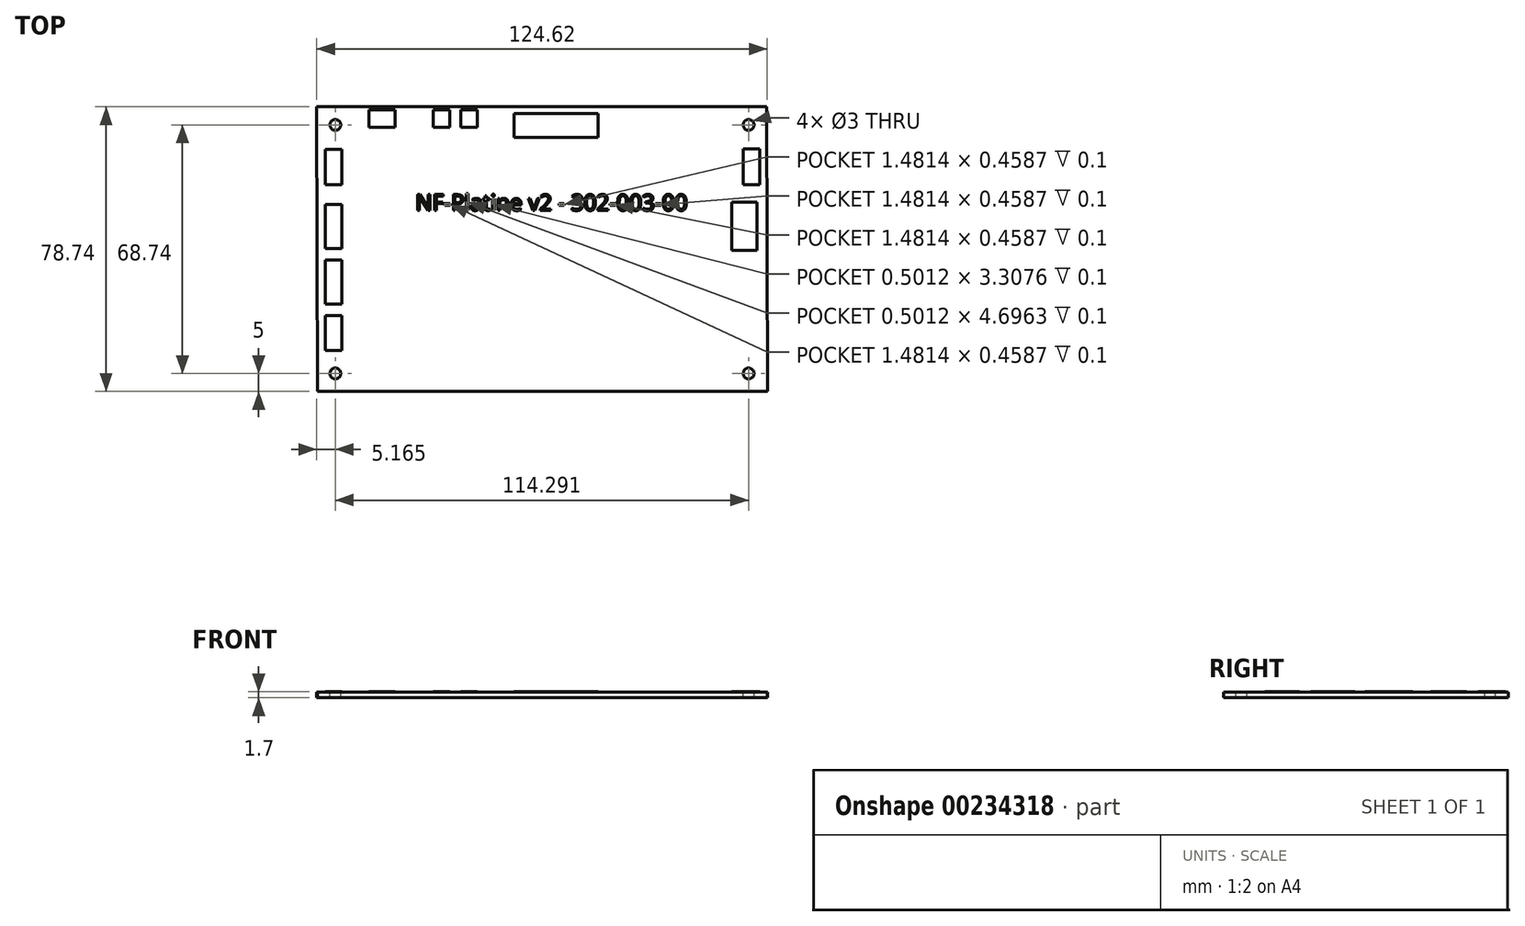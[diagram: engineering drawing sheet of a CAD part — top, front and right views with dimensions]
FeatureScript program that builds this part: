
annotation { "Feature Type Name" : "Feature", "Feature Type Description" : "" }
export const myFeature = defineFeature(function(context is Context, id is Id, definition is map)
    precondition{}
    {
        {
            var Q0;
            Q0=qCreatedBy(makeId("Top.planeOp"),FACE);
            var sketch = newSketch(context, id + "F0", { "sketchPlane" : qUnion([Q0])});
            skLineSegment(sketch, "E0.bottom", {"start": v(62.31, -39.37) * mm, "end": v(-62.15, -39.37) * mm});
            skLineSegment(sketch, "E0.top", {"start": v(62.15, 39.37) * mm, "end": v(-62.31, 39.37) * mm});
            skLineSegment(sketch, "E0.left", {"start": v(62.31, -39.37) * mm, "end": v(62.15, 39.37) * mm});
            skLineSegment(sketch, "E0.right", {"start": v(-62.15, -39.37) * mm, "end": v(-62.31, 39.37) * mm});
            skPoint(sketch, "E0.middle", {"position": v(0, 0) * mm});
            skCircle(sketch, "E1", {"center": v(-57.15, -34.37) * mm, "radius": 1.5 * mm});
            skCircle(sketch, "E2.MirrorC", {"center": v(57.15, -34.37) * mm, "radius": 1.5 * mm});
            skCircle(sketch, "E3.MirrorC", {"center": v(-57.15, 34.37) * mm, "radius": 1.5 * mm});
            skCircle(sketch, "E4.MirrorC", {"center": v(57.15, 34.37) * mm, "radius": 1.5 * mm});
            skLineSegment(sketch, "E5.bottom", {"start": v(-59.91, 27.62) * mm, "end": v(-55.3, 27.62) * mm});
            skLineSegment(sketch, "E5.top", {"start": v(-59.91, 17.86) * mm, "end": v(-55.3, 17.86) * mm});
            skLineSegment(sketch, "E5.left", {"start": v(-59.91, 27.62) * mm, "end": v(-59.91, 17.86) * mm});
            skLineSegment(sketch, "E5.right", {"start": v(-55.3, 27.62) * mm, "end": v(-55.3, 17.86) * mm});
            skLineSegment(sketch, "E6.bottom", {"start": v(-59.91, 12.38) * mm, "end": v(-55.3, 12.38) * mm});
            skLineSegment(sketch, "E6.top", {"start": v(-59.91, 0.12) * mm, "end": v(-55.3, 0.12) * mm});
            skLineSegment(sketch, "E6.left", {"start": v(-59.91, 12.38) * mm, "end": v(-59.91, 0.12) * mm});
            skLineSegment(sketch, "E6.right", {"start": v(-55.3, 12.38) * mm, "end": v(-55.3, 0.12) * mm});
            skLineSegment(sketch, "E7.bottom", {"start": v(-59.91, -3) * mm, "end": v(-55.3, -3) * mm});
            skLineSegment(sketch, "E7.top", {"start": v(-59.91, -15.22) * mm, "end": v(-55.3, -15.22) * mm});
            skLineSegment(sketch, "E7.left", {"start": v(-59.91, -3) * mm, "end": v(-59.91, -15.22) * mm});
            skLineSegment(sketch, "E7.right", {"start": v(-55.3, -3) * mm, "end": v(-55.3, -15.22) * mm});
            skLineSegment(sketch, "E8.bottom", {"start": v(-59.91, -18.36) * mm, "end": v(-55.3, -18.36) * mm});
            skLineSegment(sketch, "E8.top", {"start": v(-59.91, -27.98) * mm, "end": v(-55.3, -27.98) * mm});
            skLineSegment(sketch, "E8.left", {"start": v(-59.91, -18.36) * mm, "end": v(-59.91, -27.98) * mm});
            skLineSegment(sketch, "E8.right", {"start": v(-55.3, -18.36) * mm, "end": v(-55.3, -27.98) * mm});
            skLineSegment(sketch, "E9.bottom", {"start": v(-47.83, 38.6) * mm, "end": v(-40.65, 38.6) * mm});
            skLineSegment(sketch, "E9.top", {"start": v(-47.83, 33.77) * mm, "end": v(-40.65, 33.77) * mm});
            skLineSegment(sketch, "E9.left", {"start": v(-47.83, 38.6) * mm, "end": v(-47.83, 33.77) * mm});
            skLineSegment(sketch, "E9.right", {"start": v(-40.65, 38.6) * mm, "end": v(-40.65, 33.77) * mm});
            skLineSegment(sketch, "E10.bottom", {"start": v(-30.04, 38.6) * mm, "end": v(-25.46, 38.6) * mm});
            skLineSegment(sketch, "E10.top", {"start": v(-30.04, 33.77) * mm, "end": v(-25.46, 33.77) * mm});
            skLineSegment(sketch, "E10.left", {"start": v(-30.04, 38.6) * mm, "end": v(-30.04, 33.77) * mm});
            skLineSegment(sketch, "E10.right", {"start": v(-25.46, 38.6) * mm, "end": v(-25.46, 33.77) * mm});
            skLineSegment(sketch, "E11.bottom", {"start": v(-22.44, 38.6) * mm, "end": v(-17.86, 38.6) * mm});
            skLineSegment(sketch, "E11.top", {"start": v(-22.44, 33.77) * mm, "end": v(-17.86, 33.77) * mm});
            skLineSegment(sketch, "E11.left", {"start": v(-22.44, 38.6) * mm, "end": v(-22.44, 33.77) * mm});
            skLineSegment(sketch, "E11.right", {"start": v(-17.86, 38.6) * mm, "end": v(-17.86, 33.77) * mm});
            skLineSegment(sketch, "E12.bottom", {"start": v(15.53, 30.95) * mm, "end": v(-7.67, 30.95) * mm});
            skLineSegment(sketch, "E12.top", {"start": v(15.53, 37.47) * mm, "end": v(-7.67, 37.47) * mm});
            skLineSegment(sketch, "E12.left", {"start": v(15.53, 30.95) * mm, "end": v(15.53, 37.47) * mm});
            skLineSegment(sketch, "E12.right", {"start": v(-7.67, 30.95) * mm, "end": v(-7.67, 37.47) * mm});
            skLineSegment(sketch, "E13.bottom", {"start": v(55.65, 27.78) * mm, "end": v(60.23, 27.78) * mm});
            skLineSegment(sketch, "E13.top", {"start": v(55.65, 17.86) * mm, "end": v(60.23, 17.86) * mm});
            skLineSegment(sketch, "E13.left", {"start": v(55.65, 27.78) * mm, "end": v(55.65, 17.86) * mm});
            skLineSegment(sketch, "E13.right", {"start": v(60.23, 27.78) * mm, "end": v(60.23, 17.86) * mm});
            skLineSegment(sketch, "E14.bottom", {"start": v(52.5, 13.03) * mm, "end": v(59.41, 13.03) * mm});
            skLineSegment(sketch, "E14.top", {"start": v(52.5, -0.3) * mm, "end": v(59.41, -0.3) * mm});
            skLineSegment(sketch, "E14.left", {"start": v(52.5, 13.03) * mm, "end": v(52.5, -0.3) * mm});
            skLineSegment(sketch, "E14.right", {"start": v(59.41, 13.03) * mm, "end": v(59.41, -0.3) * mm});
            skSolve(sketch);
        }
        {
            var Q0;
            Q0=makeQuery(id+"F0.imprint","IMPRINT",FACE,{"disambiguationData":[TD([[makeQuery(id+"F0.imprint","IMPRINT",EDGE,{"derivedFrom":sQuery(id+"F0.wireOp",EDGE,"E0.bottom")}),-1.0]])]});
            var Q1;
            Q1=makeQuery(id+"F0.imprint","IMPRINT",FACE,{"disambiguationData":[TD([[makeQuery(id+"F0.imprint","IMPRINT",EDGE,{"derivedFrom":sQuery(id+"F0.wireOp",EDGE,"E5.bottom")}),-1.0]])]});
            var Q2;
            Q2=makeQuery(id+"F0.imprint","IMPRINT",FACE,{"disambiguationData":[TD([[makeQuery(id+"F0.imprint","IMPRINT",EDGE,{"derivedFrom":sQuery(id+"F0.wireOp",EDGE,"E6.bottom")}),-1.0]])]});
            var Q3;
            Q3=makeQuery(id+"F0.imprint","IMPRINT",FACE,{"disambiguationData":[TD([[makeQuery(id+"F0.imprint","IMPRINT",EDGE,{"derivedFrom":sQuery(id+"F0.wireOp",EDGE,"E7.bottom")}),-1.0]])]});
            var Q4;
            Q4=makeQuery(id+"F0.imprint","IMPRINT",FACE,{"disambiguationData":[TD([[makeQuery(id+"F0.imprint","IMPRINT",EDGE,{"derivedFrom":sQuery(id+"F0.wireOp",EDGE,"E8.bottom")}),-1.0]])]});
            var Q5;
            Q5=makeQuery(id+"F0.imprint","IMPRINT",FACE,{"disambiguationData":[TD([[makeQuery(id+"F0.imprint","IMPRINT",EDGE,{"derivedFrom":sQuery(id+"F0.wireOp",EDGE,"E9.bottom")}),-1.0]])]});
            var Q6;
            Q6=makeQuery(id+"F0.imprint","IMPRINT",FACE,{"disambiguationData":[TD([[makeQuery(id+"F0.imprint","IMPRINT",EDGE,{"derivedFrom":sQuery(id+"F0.wireOp",EDGE,"E10.bottom")}),-1.0]])]});
            var Q7;
            Q7=makeQuery(id+"F0.imprint","IMPRINT",FACE,{"disambiguationData":[TD([[makeQuery(id+"F0.imprint","IMPRINT",EDGE,{"derivedFrom":sQuery(id+"F0.wireOp",EDGE,"E11.bottom")}),-1.0]])]});
            var Q8;
            Q8=makeQuery(id+"F0.imprint","IMPRINT",FACE,{"disambiguationData":[TD([[makeQuery(id+"F0.imprint","IMPRINT",EDGE,{"derivedFrom":sQuery(id+"F0.wireOp",EDGE,"E12.bottom")}),-1.0]])]});
            var Q9;
            Q9=makeQuery(id+"F0.imprint","IMPRINT",FACE,{"disambiguationData":[TD([[makeQuery(id+"F0.imprint","IMPRINT",EDGE,{"derivedFrom":sQuery(id+"F0.wireOp",EDGE,"E13.bottom")}),-1.0]])]});
            var Q10;
            Q10=makeQuery(id+"F0.imprint","IMPRINT",FACE,{"disambiguationData":[TD([[makeQuery(id+"F0.imprint","IMPRINT",EDGE,{"derivedFrom":sQuery(id+"F0.wireOp",EDGE,"E14.bottom")}),-1.0]])]});
            extrude(context, id + "F1", {"entities" : qUnion([Q0, Q1, Q2, Q3, Q4, Q5, Q6, Q7, Q8, Q9, Q10]), "oppositeDirection" : true, "offsetDistance" : 25 * mm, "depth" : 1.6 * mm});
        }
        {
            var Q0;
            Q0=makeQuery(id+"F1.opExtrude","CAP_FACE",FACE,{"disambiguationData":[OSD([sQuery(id+"F0.wireOp",EDGE,"E0.bottom"),sQuery(id+"F0.wireOp",EDGE,"E0.top"),sQuery(id+"F0.wireOp",EDGE,"E0.left"),sQuery(id+"F0.wireOp",EDGE,"E0.right"),sQuery(id+"F0.wireOp",EDGE,"E1"),sQuery(id+"F0.wireOp",EDGE,"E2.MirrorC")])],"isStart":true});
            var sketch = newSketch(context, id + "F2", { "sketchPlane" : qUnion([Q0])});
            skText(sketch, "E15", { "text": "NF-Platine v2 - 302-003-00", "fontName": "OpenSans-Regular.ttf"});
            const initialGuessF2  = {"E15": [-0.035, 0.0107, 1, 0, 0.00445]};
            skSetInitialGuess(sketch, initialGuessF2);
            skSolve(sketch);
        }
        {
            var Q0;
            Q0 = qSketchRegion(id + "F2", true);
            extrude(context, id + "F3", {"entities" : qUnion([Q0]), "operationType" : NewBodyOperationType.REMOVE, "oppositeDirection" : true, "depth" : .1 * mm});
        }
        {
            var Q0;
            Q0=makeQuery(id+"F0.imprint","IMPRINT",FACE,{"disambiguationData":[TD([[makeQuery(id+"F0.imprint","IMPRINT",EDGE,{"derivedFrom":sQuery(id+"F0.wireOp",EDGE,"E5.bottom")}),-1.0]])]});
            var Q1;
            Q1=makeQuery(id+"F0.imprint","IMPRINT",FACE,{"disambiguationData":[TD([[makeQuery(id+"F0.imprint","IMPRINT",EDGE,{"derivedFrom":sQuery(id+"F0.wireOp",EDGE,"E6.bottom")}),-1.0]])]});
            var Q2;
            Q2=makeQuery(id+"F0.imprint","IMPRINT",FACE,{"disambiguationData":[TD([[makeQuery(id+"F0.imprint","IMPRINT",EDGE,{"derivedFrom":sQuery(id+"F0.wireOp",EDGE,"E7.bottom")}),-1.0]])]});
            var Q3;
            Q3=makeQuery(id+"F0.imprint","IMPRINT",FACE,{"disambiguationData":[TD([[makeQuery(id+"F0.imprint","IMPRINT",EDGE,{"derivedFrom":sQuery(id+"F0.wireOp",EDGE,"E8.bottom")}),-1.0]])]});
            var Q4;
            Q4=makeQuery(id+"F0.imprint","IMPRINT",FACE,{"disambiguationData":[TD([[makeQuery(id+"F0.imprint","IMPRINT",EDGE,{"derivedFrom":sQuery(id+"F0.wireOp",EDGE,"E9.bottom")}),-1.0]])]});
            var Q5;
            Q5=makeQuery(id+"F0.imprint","IMPRINT",FACE,{"disambiguationData":[TD([[makeQuery(id+"F0.imprint","IMPRINT",EDGE,{"derivedFrom":sQuery(id+"F0.wireOp",EDGE,"E10.bottom")}),-1.0]])]});
            var Q6;
            Q6=makeQuery(id+"F0.imprint","IMPRINT",FACE,{"disambiguationData":[TD([[makeQuery(id+"F0.imprint","IMPRINT",EDGE,{"derivedFrom":sQuery(id+"F0.wireOp",EDGE,"E11.bottom")}),-1.0]])]});
            var Q7;
            Q7=makeQuery(id+"F0.imprint","IMPRINT",FACE,{"disambiguationData":[TD([[makeQuery(id+"F0.imprint","IMPRINT",EDGE,{"derivedFrom":sQuery(id+"F0.wireOp",EDGE,"E12.bottom")}),-1.0]])]});
            var Q8;
            Q8=makeQuery(id+"F0.imprint","IMPRINT",FACE,{"disambiguationData":[TD([[makeQuery(id+"F0.imprint","IMPRINT",EDGE,{"derivedFrom":sQuery(id+"F0.wireOp",EDGE,"E14.bottom")}),-1.0]])]});
            var Q9;
            Q9=makeQuery(id+"F0.imprint","IMPRINT",FACE,{"disambiguationData":[TD([[makeQuery(id+"F0.imprint","IMPRINT",EDGE,{"derivedFrom":sQuery(id+"F0.wireOp",EDGE,"E13.bottom")}),-1.0]])]});
            extrude(context, id + "F4", {"entities" : qUnion([Q0, Q1, Q2, Q3, Q4, Q5, Q6, Q7, Q8, Q9]), "operationType" : NewBodyOperationType.ADD, "depth" : .1 * mm, "offsetDistance" : 25 * mm});
        }
    });
